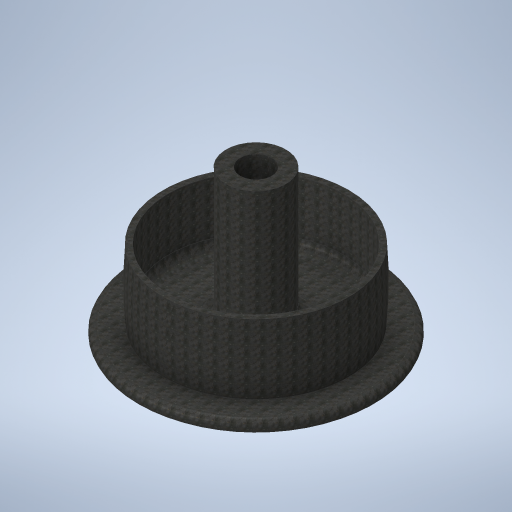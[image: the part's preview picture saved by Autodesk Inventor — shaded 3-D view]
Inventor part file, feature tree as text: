
AUTODESK INVENTOR PART (.ipt)
format: ipt  version: 2024 (Build 280153000, 153)  size: 404,992 bytes
history: native  units: in
note: dims shown in document units (in); Inventor stores cm internally (conversion verified against a paired STEP export)
features: sketch x2, revolve x1, extrude x1
ambient origin geometry x8: Origin, YZ Plane, XZ Plane, XY Plane, X Axis, Y Axis, Z Axis, Center Point
bodies: Solid1 (feature_tree)
feature tree (4):
  revolve  "Revolution1"  [1 undecoded]
  extrude  "Extrusion1"  Depth=73.0in
  sketch  "Sketch1"  dims[d0=36.0in d3=40.0in]
  sketch  "Sketch2"  dims[d5=93.0in d6=73.0in d8=3.0in d10=8.0in d11=19.0in d12=143.0in d13=105.0in d14=12.0in d15=6.0in d18=250.0in d19=113.06in d20=14.3959in d21=9.9827in d23=3.0in d26=111.5367in d27=90.0deg d28=28.0in d29=73.0in d30=0.0in d31=50.0in]
note: 1 required parameter value undecoded (feature->parameter linkage not recoverable at this tier; creation-order binding heuristic only, values carry confidence <= 0.55)
